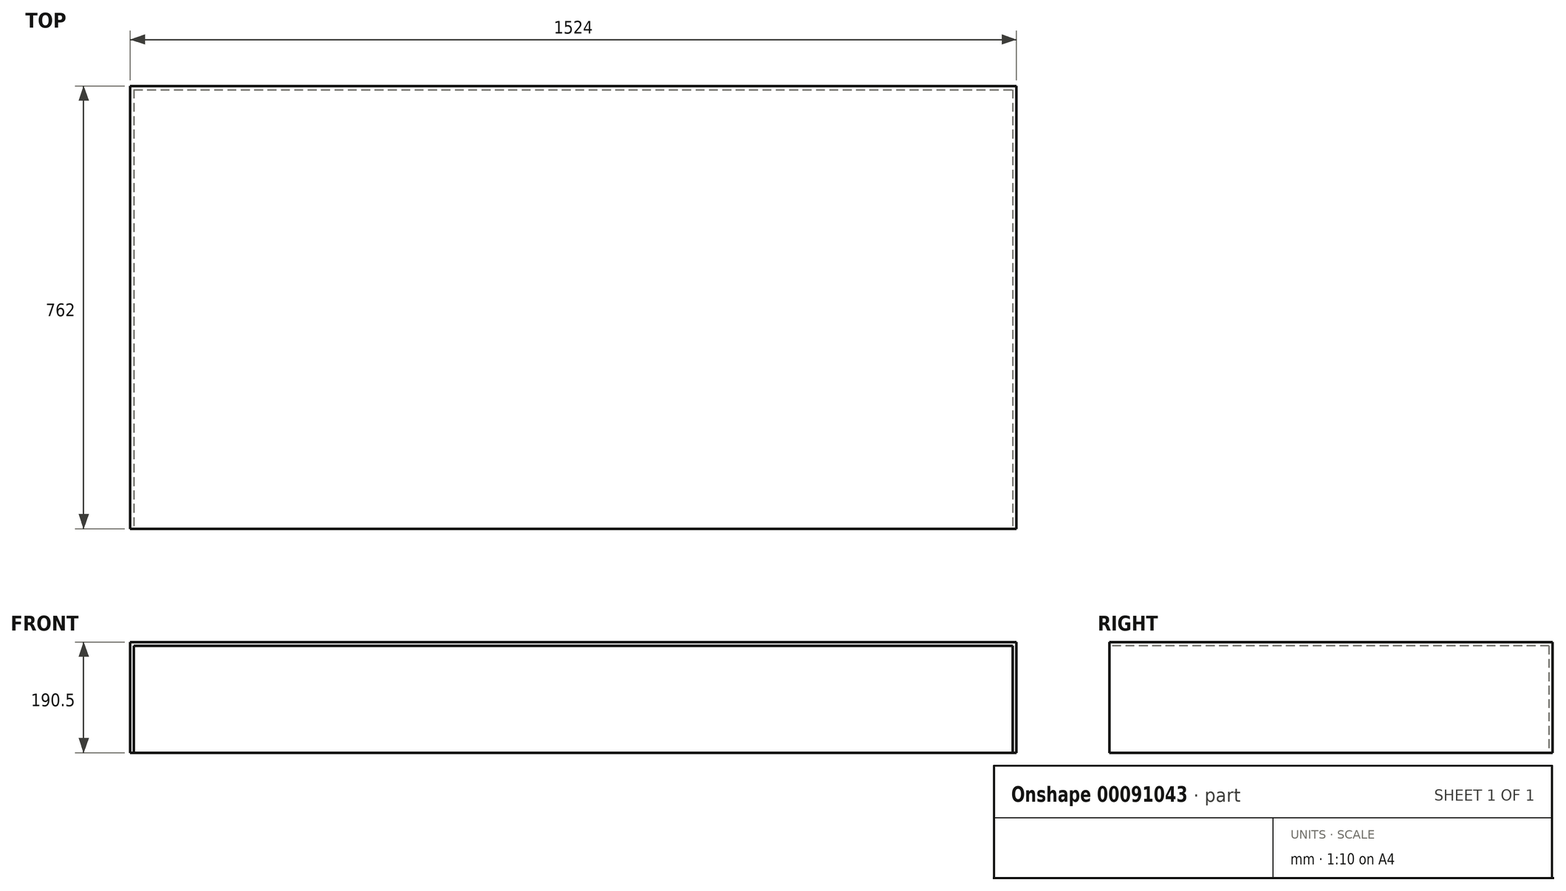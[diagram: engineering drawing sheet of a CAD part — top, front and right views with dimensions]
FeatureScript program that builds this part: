
annotation { "Feature Type Name" : "Feature", "Feature Type Description" : "" }
export const myFeature = defineFeature(function(context is Context, id is Id, definition is map)
    precondition{}
    {
        {
            var Q0;
            Q0=qCreatedBy(makeId("Top.planeOp"),FACE);
            var sketch = newSketch(context, id + "F0", { "sketchPlane" : qUnion([Q0])});
            skLineSegment(sketch, "E0.bottom", {"start": v(-720.8, 510.84) * mm, "end": v(803.2, 510.84) * mm});
            skLineSegment(sketch, "E0.top", {"start": v(-720.8, -251.16) * mm, "end": v(803.2, -251.16) * mm});
            skLineSegment(sketch, "E0.left", {"start": v(-720.8, 510.84) * mm, "end": v(-720.8, -251.16) * mm});
            skLineSegment(sketch, "E0.right", {"start": v(803.2, 510.84) * mm, "end": v(803.2, -251.16) * mm});
            skSolve(sketch);
        }
        {
            var Q0;
            Q0=makeQuery(id+"F0.imprint","IMPRINT",FACE,{"disambiguationData":[TD([[makeQuery(id+"F0.imprint","IMPRINT",EDGE,{"derivedFrom":sQuery(id+"F0.wireOp",EDGE,"E0.bottom")}),-1.0]])]});
            extrude(context, id + "F1", {"entities" : qUnion([Q0]), "depth" : 190.5 * mm});
        }
        {
            var Q0;
            Q0=makeQuery(id+"F1.opExtrude","CAP_FACE",FACE,{"disambiguationData":[OSD([sQuery(id+"F0.wireOp",EDGE,"E0.bottom"),sQuery(id+"F0.wireOp",EDGE,"E0.top"),sQuery(id+"F0.wireOp",EDGE,"E0.left"),sQuery(id+"F0.wireOp",EDGE,"E0.right")])],"isStart":true});
            shell(context, id + "F2", {"entities" : qUnion([Q0]), "thickness" : 6.35 * mm});
        }
        {
            var Q0;
            Q0=makeQuery(id+"F2.opShell","OFFSET_FACE",FACE,{"disambiguationData":[OSD([sQuery(id+"F0.wireOp",EDGE,"E0.top")])]});
            var sketch = newSketch(context, id + "F3", { "sketchPlane" : qUnion([Q0])});
            skLineSegment(sketch, "E1", {"start": v(714.45, 184.15) * mm, "end": v(714.45, 0) * mm});
            skLineSegment(sketch, "E2", {"start": v(714.45, 0) * mm, "end": v(-796.85, 0) * mm});
            skLineSegment(sketch, "E3", {"start": v(-796.85, 0) * mm, "end": v(-796.85, 184.15) * mm});
            skLineSegment(sketch, "E4", {"start": v(-796.85, 184.15) * mm, "end": v(714.45, 184.15) * mm});
            skSolve(sketch);
        }
        {
            var Q0;
            Q0 = qSketchRegion(id + "F3", true);
            extrude(context, id + "F4", {"entities" : qUnion([Q0]), "operationType" : NewBodyOperationType.REMOVE, "oppositeDirection" : true, "depth" : 25.4 * mm});
        }
    });
